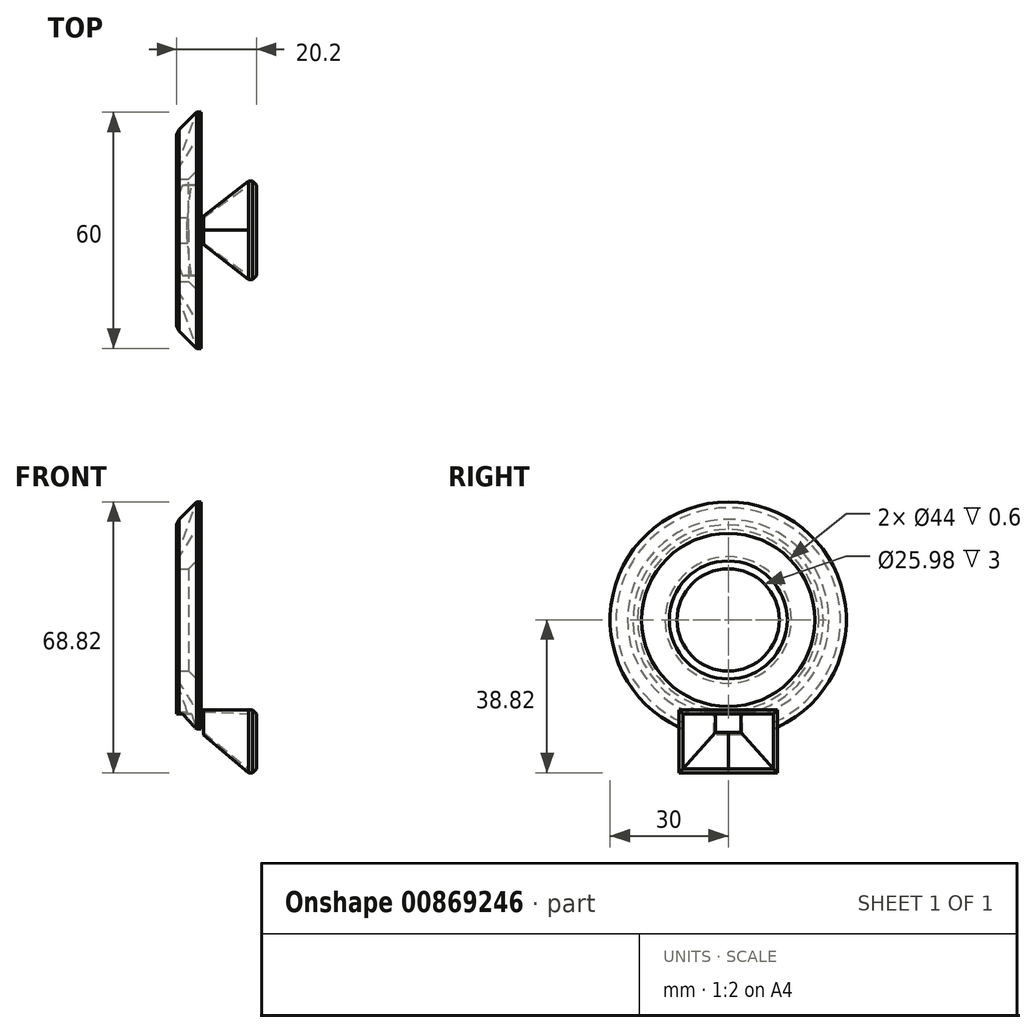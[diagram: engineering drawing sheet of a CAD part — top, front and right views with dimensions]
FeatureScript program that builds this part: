
annotation { "Feature Type Name" : "Feature", "Feature Type Description" : "" }
export const myFeature = defineFeature(function(context is Context, id is Id, definition is map)
    precondition{}
    {
        {
            var Q0;
            Q0=qCreatedBy(makeId("Front.planeOp"),FACE);
            var sketch = newSketch(context, id + "F0", { "sketchPlane" : qUnion([Q0])});
            skLineSegment(sketch, "E0.bottom", {"start": v(-2.5, 15) * mm, "end": v(2.5, 15) * mm});
            skLineSegment(sketch, "E0.top", {"start": v(-2.5, -15) * mm, "end": v(2.5, -15) * mm});
            skLineSegment(sketch, "E0.left", {"start": v(-2.5, 15) * mm, "end": v(-2.5, -15) * mm});
            skLineSegment(sketch, "E0.right", {"start": v(2.5, 15) * mm, "end": v(2.5, -15) * mm});
            skPoint(sketch, "E0.middle", {"position": v(0, 0) * mm});
            skLineSegment(sketch, "E1", {"start": v(2.5, 23) * mm, "end": v(2.5, 15) * mm});
            skLineSegment(sketch, "E2", {"start": v(-8.2, -15) * mm, "end": v(-8.2, 23) * mm});
            skLineSegment(sketch, "E3", {"start": v(2.5, 23) * mm, "end": v(-2.5, 15) * mm});
            skLineSegment(sketch, "E4", {"start": v(-2.5, 15) * mm, "end": v(-2.5, 30) * mm});
            skLineSegment(sketch, "E5", {"start": v(-2.5, 16.07) * mm, "end": v(2.5, 30) * mm});
            skLineSegment(sketch, "E6", {"start": v(-2.5, 30) * mm, "end": v(2.5, 30) * mm});
            skLineSegment(sketch, "E7", {"start": v(2.5, 0) * mm, "end": v(-2.5, 0) * mm});
            skLineSegment(sketch, "E8.bottom", {"start": v(2.5, 15) * mm, "end": v(-2.5, 15) * mm});
            skLineSegment(sketch, "E8.top", {"start": v(2.5, 12.99) * mm, "end": v(-2.5, 12.99) * mm});
            skLineSegment(sketch, "E8.left", {"start": v(2.5, 15) * mm, "end": v(2.5, 12.99) * mm});
            skLineSegment(sketch, "E8.right", {"start": v(-2.5, 15) * mm, "end": v(-2.5, 12.99) * mm});
            skSolve(sketch);
        }
        {
            var Q0;
            {var subQ0=sQuery(id+"F0.wireOp",EDGE,"E5");Q0=makeQuery(id+"F0.imprint","IMPRINT",FACE,{"disambiguationData":[TD([[makeQuery(id+"F0.imprint","IMPRINT",EDGE,{"derivedFrom":subQ0}),1.0]])]});}
            var Q1;
            Q1=makeQuery(id+"F0.imprint","IMPRINT",FACE,{"disambiguationData":[TD([[makeQuery(id+"F0.imprint","IMPRINT",EDGE,{"derivedFrom":sQuery(id+"F0.wireOp",EDGE,"E0.bottom")}),1.0]])]});
            var Q2;
            {var subQ0=sQuery(id+"F0.wireOp",EDGE,"E0.bottom");Q2=makeQuery(id+"F0.imprint","IMPRINT",FACE,{"disambiguationData":[TD([[makeQuery(id+"F0.imprint","IMPRINT",EDGE,{"derivedFrom":subQ0}),-1.0]])]});}
            var Q3;
            Q3=makeQuery(id+"F0.imprint","IMPRINT",FACE,{"disambiguationData":[TD([[makeQuery(id+"F0.imprint","IMPRINT",EDGE,{"derivedFrom":sQuery(id+"F0.wireOp",EDGE,"E0.bottom")}),1.0]])]});
            var Q4;
            Q4=sQuery(id+"F0.wireOp",EDGE,"E7");
            revolve(context, id + "F1", {"surfaceOperationType" : NewSurfaceOperationType.NEW, "entities" : qUnion([Q0, Q1, Q2, Q3]), "axis" : qUnion([Q4]), "revolveType" : RevolveType.FULL});
        }
        {
            var Q0;
            Q0=makeQuery(id+"F1.opRevolve","SWEPT_EDGE",EDGE,{"disambiguationData":[OSD([sQuery(id+"F0.wireOp",EDGE,"E4"),sQuery(id+"F0.wireOp",EDGE,"E6")])]});
            chamfer(context, id + "F2", {"entities" : qUnion([Q0]), "width" : 5 * mm, "tangentPropagation" : true});
        }
        {
            var Q0;
            Q0=makeQuery(id+"F1.opRevolve","SWEPT_EDGE",EDGE,{"disambiguationData":[OSD([sQuery(id+"F0.wireOp",EDGE,"E0.right"),sQuery(id+"F0.wireOp",EDGE,"E8.top")])]});
            chamfer(context, id + "F3", {"entities" : qUnion([Q0]), "width" : 2 * mm, "tangentPropagation" : true});
        }
        {
            var Q0;
            {var subQ0=sQuery(id+"F0.wireOp",EDGE,"E4");Q0=makeQuery(id+"F2.opChamfer","BLEND_EDGE",EDGE,{"blendedFrom":[makeQuery(id+"F1.opRevolve","SWEPT_EDGE",EDGE,{"disambiguationData":[OSD([subQ0,sQuery(id+"F0.wireOp",EDGE,"E6")])]}),makeQuery(id+"F1.opRevolve","SWEPT_FACE",FACE,{"disambiguationData":[OSD([subQ0])]})],"blendedInto":[makeQuery(id+"F1.opRevolve","SWEPT_FACE",FACE,{"disambiguationData":[OSD([subQ0])]})]});}
            chamfer(context, id + "F4", {"entities" : qUnion([Q0]), "width" : 2 * mm, "tangentPropagation" : true});
        }
        {
            var Q0;
            Q0=makeQuery(id+"F1.opRevolve","SWEPT_FACE",FACE,{"disambiguationData":[OSD([sQuery(id+"F0.wireOp",EDGE,"E0.right"),sQuery(id+"F0.wireOp",EDGE,"E1")])]});
            var sketch = newSketch(context, id + "F5", { "sketchPlane" : qUnion([Q0])});
            skCircle(sketch, "E9", {"center": v(0, 0) * mm, "radius": 23 * mm});
            skCircle(sketch, "E10", {"center": v(0, 0) * mm, "radius": 22 * mm});
            skCircle(sketch, "E11", {"center": v(0, 0) * mm, "radius": 30 * mm});
            skCircle(sketch, "E12", {"center": v(0, 0) * mm, "radius": 28.5 * mm});
            skSolve(sketch);
        }
        {
            var Q0;
            Q0=makeQuery(id+"F5.imprint","IMPRINT",FACE,{"disambiguationData":[TD([[makeQuery(id+"F5.imprint","IMPRINT",EDGE,{"derivedFrom":sQuery(id+"F5.wireOp",EDGE,"E9")}),1.0]])]});
            var Q1;
            Q1=makeQuery(id+"F5.imprint","IMPRINT",FACE,{"disambiguationData":[TD([[makeQuery(id+"F5.imprint","IMPRINT",EDGE,{"derivedFrom":sQuery(id+"F5.wireOp",EDGE,"E11")}),1.0]])]});
            extrude(context, id + "F6", {"entities" : qUnion([Q0, Q1]), "operationType" : NewBodyOperationType.ADD, "depth" : .6 * mm, "offsetDistance" : 25 * mm});
        }
        {
            var Q0;
            Q0=makeQuery(id+"F6.opExtrude","CAP_FACE",FACE,{"disambiguationData":[OSD([sQuery(id+"F5.wireOp",EDGE,"E9"),sQuery(id+"F5.wireOp",EDGE,"E10")])],"isStart":false});
            var sketch = newSketch(context, id + "F7", { "sketchPlane" : qUnion([Q0])});
            skCircle(sketch, "E13", {"center": v(0, 0) * mm, "radius": 30 * mm});
            skCircle(sketch, "E14", {"center": v(0, 0) * mm, "radius": 22 * mm});
            skSolve(sketch);
        }
        {
            var Q0;
            Q0=qSketchRegion(id+"F7",true);
            extrude(context, id + "F8", {"entities" : qUnion([Q0]), "depth" : .6 * mm, "offsetDistance" : 25 * mm});
        }
        {
            var Q0;
            Q0=makeQuery(id+"F8.opExtrude","CAP_FACE",FACE,{"disambiguationData":[OSD([sQuery(id+"F7.wireOp",EDGE,"E13"),sQuery(id+"F7.wireOp",EDGE,"E14")])],"isStart":false});
            var sketch = newSketch(context, id + "F9", { "sketchPlane" : qUnion([Q0])});
            skLineSegment(sketch, "E15", {"start": v(0, -30) * mm, "end": v(0, -22) * mm});
            skLineSegment(sketch, "E16.bottom", {"start": v(3.6, -29.18) * mm, "end": v(-3.6, -29.18) * mm});
            skLineSegment(sketch, "E16.top", {"start": v(3.6, -22.82) * mm, "end": v(-3.6, -22.82) * mm});
            skLineSegment(sketch, "E16.left", {"start": v(3.6, -29.18) * mm, "end": v(3.6, -22.82) * mm});
            skLineSegment(sketch, "E16.right", {"start": v(-3.6, -29.18) * mm, "end": v(-3.6, -22.82) * mm});
            skPoint(sketch, "E16.middle", {"position": v(0, -26) * mm});
            skSolve(sketch);
        }
        {
            var Q0;
            Q0=qSketchRegion(id+"F9",true);
            extrude(context, id + "F10", {"entities" : qUnion([Q0]), "operationType" : NewBodyOperationType.ADD, "depth" : .6 * mm, "offsetDistance" : 25 * mm});
        }
        {
            var Q0;
            Q0=makeQuery(id+"F10.opExtrude","SWEPT_FACE",FACE,{"disambiguationData":[OSD([sQuery(id+"F9.wireOp",EDGE,"E16.top")])]});
            var sketch = newSketch(context, id + "F11", { "sketchPlane" : qUnion([Q0])});
            skLineSegment(sketch, "E17.bottom", {"start": v(17.44, -6.08) * mm, "end": v(-9.45, -6.08) * mm});
            skLineSegment(sketch, "E17.top", {"start": v(17.44, 12.53) * mm, "end": v(-9.45, 12.53) * mm});
            skLineSegment(sketch, "E17.left", {"start": v(17.44, -6.08) * mm, "end": v(17.44, 12.53) * mm});
            skLineSegment(sketch, "E17.right", {"start": v(-9.45, -6.08) * mm, "end": v(-9.45, 12.53) * mm});
            skPoint(sketch, "E17.middle", {"position": v(4, 3.23) * mm});
            skLineSegment(sketch, "E18", {"start": v(3.7, 0) * mm, "end": v(16.7, 0) * mm});
            skLineSegment(sketch, "E19.bottom", {"start": v(15.7, 12.5) * mm, "end": v(17.7, 12.5) * mm});
            skLineSegment(sketch, "E19.top", {"start": v(15.7, -12.5) * mm, "end": v(17.7, -12.5) * mm});
            skLineSegment(sketch, "E19.left", {"start": v(15.7, 12.5) * mm, "end": v(15.7, -12.5) * mm});
            skLineSegment(sketch, "E19.right", {"start": v(17.7, 12.5) * mm, "end": v(17.7, -12.5) * mm});
            skPoint(sketch, "E19.middle", {"position": v(16.7, 0) * mm});
            skSolve(sketch);
        }
        {
            var Q0;
            {var subQ3=sQuery(id+"F11.wireOp",EDGE,"E19.bottom");Q0=makeQuery(id+"F11.imprint","IMPRINT",FACE,{"disambiguationData":[TD([[makeQuery(id+"F11.imprint","IMPRINT",EDGE,{"derivedFrom":subQ3}),-1.0]])]});}
            var Q1;
            {var subQ5=sQuery(id+"F11.wireOp",EDGE,"E19.top");Q1=makeQuery(id+"F11.imprint","IMPRINT",FACE,{"disambiguationData":[TD([[makeQuery(id+"F11.imprint","IMPRINT",EDGE,{"derivedFrom":subQ5}),1.0]])]});}
            extrude(context, id + "F12", {"entities" : qUnion([Q0, Q1]), "operationType" : NewBodyOperationType.ADD, "depth" : -16 * mm, "offsetDistance" : 25 * mm});
        }
        {
            var Q0;
            Q0=makeQuery(id+"F10.opExtrude","CAP_FACE",FACE,{"disambiguationData":[OSD([sQuery(id+"F9.wireOp",EDGE,"E16.bottom"),sQuery(id+"F9.wireOp",EDGE,"E16.top"),sQuery(id+"F9.wireOp",EDGE,"E16.left"),sQuery(id+"F9.wireOp",EDGE,"E16.right")])],"isStart":false});
            var sketch = newSketch(context, id + "F13", { "sketchPlane" : qUnion([Q0])});
            skLineSegment(sketch, "E20", {"start": v(0, -22.82) * mm, "end": v(0, -29.18) * mm});
            skLineSegment(sketch, "E21.bottom", {"start": v(-3.23, -28.62) * mm, "end": v(3.23, -28.62) * mm});
            skLineSegment(sketch, "E21.top", {"start": v(-3.23, -23.38) * mm, "end": v(3.23, -23.38) * mm});
            skLineSegment(sketch, "E21.left", {"start": v(-3.23, -28.62) * mm, "end": v(-3.23, -23.38) * mm});
            skLineSegment(sketch, "E21.right", {"start": v(3.23, -28.62) * mm, "end": v(3.23, -23.38) * mm});
            skPoint(sketch, "E21.middle", {"position": v(0, -26) * mm});
            skSolve(sketch);
        }
        {
            var Q0;
            Q0=makeQuery(id+"F12.opExtrude","SWEPT_FACE",FACE,{"disambiguationData":[OSD([sQuery(id+"F11.wireOp",EDGE,"E19.left")])]});
            var sketch = newSketch(context, id + "F14", { "sketchPlane" : qUnion([Q0])});
            skLineSegment(sketch, "E22", {"start": v(0, -38.82) * mm, "end": v(0, -22.82) * mm});
            skLineSegment(sketch, "E23.bottom", {"start": v(11.5, -37.82) * mm, "end": v(-11.5, -37.82) * mm});
            skLineSegment(sketch, "E23.top", {"start": v(11.5, -23.82) * mm, "end": v(-11.5, -23.82) * mm});
            skLineSegment(sketch, "E23.left", {"start": v(11.5, -37.82) * mm, "end": v(11.5, -23.82) * mm});
            skLineSegment(sketch, "E23.right", {"start": v(-11.5, -37.82) * mm, "end": v(-11.5, -23.82) * mm});
            skPoint(sketch, "E23.middle", {"position": v(0, -30.82) * mm});
            skSolve(sketch);
        }
        {
            var Q0;
            Q0=makeQuery(id+"F12.opExtrude","SWEPT_FACE",FACE,{"disambiguationData":[OSD([sQuery(id+"F11.wireOp",EDGE,"E19.right")])]});
            var sketch = newSketch(context, id + "F15", { "sketchPlane" : qUnion([Q0])});
            skLineSegment(sketch, "E24", {"start": v(0, -22.82) * mm, "end": v(0, -38.82) * mm});
            skLineSegment(sketch, "E25.bottom", {"start": v(-11.5, -23.82) * mm, "end": v(11.5, -23.82) * mm});
            skLineSegment(sketch, "E25.top", {"start": v(-11.5, -37.82) * mm, "end": v(11.5, -37.82) * mm});
            skLineSegment(sketch, "E25.left", {"start": v(-11.5, -23.82) * mm, "end": v(-11.5, -37.82) * mm});
            skLineSegment(sketch, "E25.right", {"start": v(11.5, -23.82) * mm, "end": v(11.5, -37.82) * mm});
            skPoint(sketch, "E25.middle", {"position": v(0, -30.82) * mm});
            skSolve(sketch);
        }
        {
            var Q0;
            {var subQ5=sQuery(id+"F15.wireOp",EDGE,"E25.right");Q0=makeQuery(id+"F15.imprint","IMPRINT",FACE,{"disambiguationData":[TD([[makeQuery(id+"F15.imprint","IMPRINT",EDGE,{"derivedFrom":subQ5}),-1.0]])]});}
            var Q1;
            {var subQ5=sQuery(id+"F15.wireOp",EDGE,"E25.left");Q1=makeQuery(id+"F15.imprint","IMPRINT",FACE,{"disambiguationData":[TD([[makeQuery(id+"F15.imprint","IMPRINT",EDGE,{"derivedFrom":subQ5}),1.0]])]});}
            extrude(context, id + "F16", {"entities" : qUnion([Q0, Q1]), "operationType" : NewBodyOperationType.REMOVE, "oppositeDirection" : true, "depth" : 25 * mm, "offsetDistance" : 25 * mm});
        }
        {
            var Q2;
            {var subQ5=sQuery(id+"F14.wireOp",EDGE,"E23.left");Q2=makeQuery(id+"F14.imprint","IMPRINT",FACE,{"disambiguationData":[TD([[makeQuery(id+"F14.imprint","IMPRINT",EDGE,{"derivedFrom":subQ5}),1.0]])]});}
            var Q3;
            {var subQ5=sQuery(id+"F13.wireOp",EDGE,"E21.left");Q3=makeQuery(id+"F13.imprint","IMPRINT",FACE,{"disambiguationData":[TD([[makeQuery(id+"F13.imprint","IMPRINT",EDGE,{"derivedFrom":subQ5}),-1.0]])]});}
            loft(context, id + "F17", {"operationType" : NewBodyOperationType.REMOVE, "sheetProfilesArray" : [{ "sheetProfileEntities" : qUnion([Q2]) }, { "sheetProfileEntities" : qUnion([Q3]) }]});
        }
        {
            var Q0;
            {var subQ5=sQuery(id+"F13.wireOp",EDGE,"E21.left");Q0=makeQuery(id+"F13.imprint","IMPRINT",FACE,{"disambiguationData":[TD([[makeQuery(id+"F13.imprint","IMPRINT",EDGE,{"derivedFrom":subQ5}),-1.0]])]});}
            var Q1;
            {var subQ5=sQuery(id+"F13.wireOp",EDGE,"E21.right");Q1=makeQuery(id+"F13.imprint","IMPRINT",FACE,{"disambiguationData":[TD([[makeQuery(id+"F13.imprint","IMPRINT",EDGE,{"derivedFrom":subQ5}),1.0]])]});}
            extrude(context, id + "F18", {"entities" : qUnion([Q0, Q1]), "operationType" : NewBodyOperationType.REMOVE, "oppositeDirection" : true, "depth" : 25 * mm, "offsetDistance" : 25 * mm});
        }
        {
            var Q0;
            {var subQ0=sQuery(id+"F13.wireOp",EDGE,"E21.left");Q0=makeQuery(id+"F13.imprint","IMPRINT",FACE,{"disambiguationData":[TD([[makeQuery(id+"F13.imprint","IMPRINT",EDGE,{"derivedFrom":subQ0}),1.0]])]});}
            var Q1;
            {var subQ0=sQuery(id+"F14.wireOp",EDGE,"E23.left");Q1=makeQuery(id+"F14.imprint","IMPRINT",FACE,{"disambiguationData":[TD([[makeQuery(id+"F14.imprint","IMPRINT",EDGE,{"derivedFrom":subQ0}),-1.0]])]});}
            loft(context, id + "F19", {"sheetProfilesArray" : [{ "sheetProfileEntities" : qUnion([Q0]) }, { "sheetProfileEntities" : qUnion([Q1]) }]});
        }
        {
            var Q0;
            {var subQ0=sQuery(id+"F13.wireOp",EDGE,"E21.right");Q0=makeQuery(id+"F13.imprint","IMPRINT",FACE,{"disambiguationData":[TD([[makeQuery(id+"F13.imprint","IMPRINT",EDGE,{"derivedFrom":subQ0}),-1.0]])]});}
            var Q1;
            {var subQ0=sQuery(id+"F14.wireOp",EDGE,"E23.right");Q1=makeQuery(id+"F14.imprint","IMPRINT",FACE,{"disambiguationData":[TD([[makeQuery(id+"F14.imprint","IMPRINT",EDGE,{"derivedFrom":subQ0}),1.0]])]});}
            loft(context, id + "F20", {"sheetProfilesArray" : [{ "sheetProfileEntities" : qUnion([Q0]) }, { "sheetProfileEntities" : qUnion([Q1]) }]});
        }
        {
            var Q0;
            Q0=makeQuery(id+"F12.opExtrude","CAP_EDGE",EDGE,{"disambiguationData":[OSD([sQuery(id+"F11.wireOp",EDGE,"E19.right")])],"isStart":true});
            var Q1;
            Q1=makeQuery(id+"F12.opExtrude","CAP_EDGE",EDGE,{"disambiguationData":[OSD([sQuery(id+"F11.wireOp",EDGE,"E19.right")])],"isStart":false});
            var Q2;
            Q2=makeQuery(id+"F12.opExtrude","SWEPT_EDGE",EDGE,{"disambiguationData":[OSD([sQuery(id+"F11.wireOp",EDGE,"E19.top"),sQuery(id+"F11.wireOp",EDGE,"E19.right")])]});
            var Q3;
            Q3=makeQuery(id+"F12.opExtrude","SWEPT_EDGE",EDGE,{"disambiguationData":[OSD([sQuery(id+"F11.wireOp",EDGE,"E19.bottom"),sQuery(id+"F11.wireOp",EDGE,"E19.right")])]});
            chamfer(context, id + "F21", {"entities" : qUnion([Q0, Q1, Q2, Q3]), "width" : 1 * mm, "tangentPropagation" : true});
        }
    });
